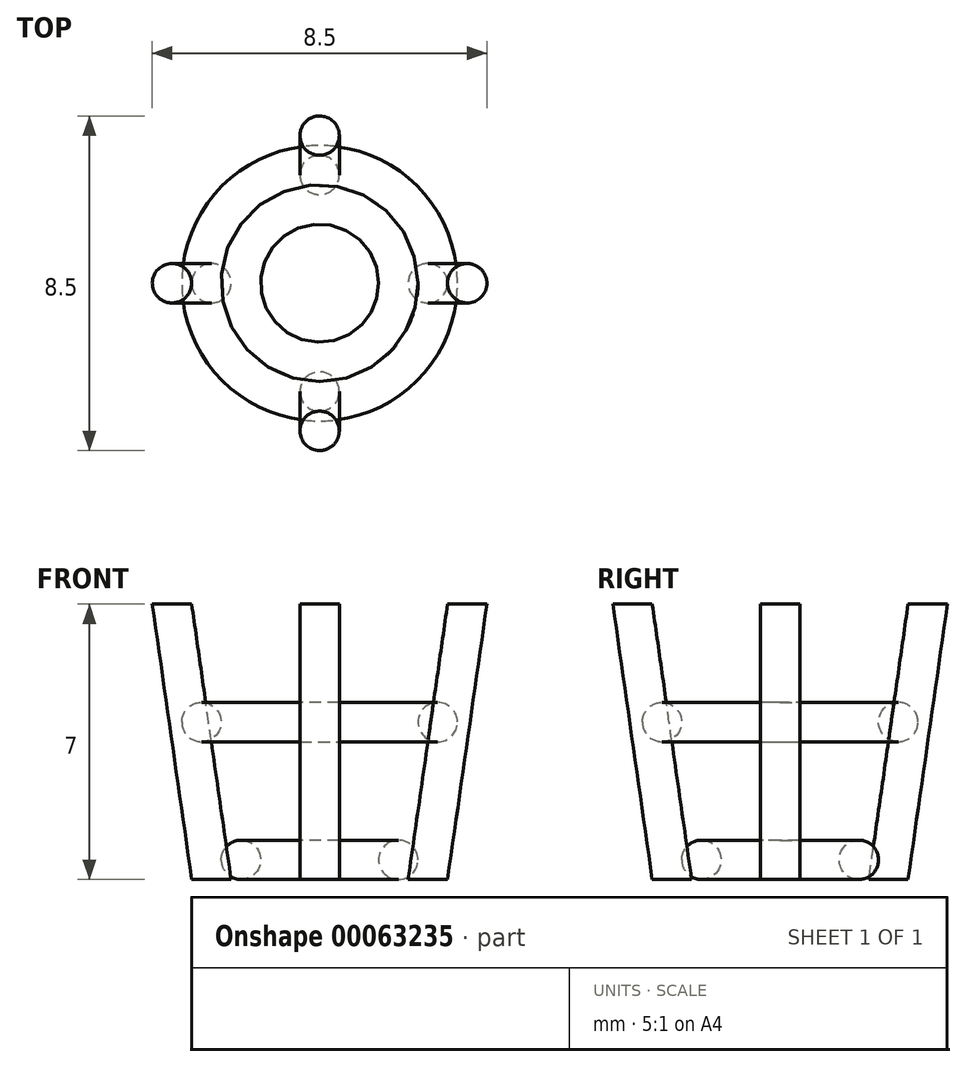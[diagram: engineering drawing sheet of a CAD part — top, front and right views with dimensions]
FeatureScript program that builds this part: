
annotation { "Feature Type Name" : "Feature", "Feature Type Description" : "" }
export const myFeature = defineFeature(function(context is Context, id is Id, definition is map)
    precondition{}
    {
        {
            var Q0;
            Q0=qCreatedBy(makeId("Front.planeOp"),FACE);
            var sketch = newSketch(context, id + "F0", { "sketchPlane" : qUnion([Q0])});
            skCircle(sketch, "E0", {"center": v(2, 0.5) * mm, "radius": 0.5 * mm});
            skCircle(sketch, "E1", {"center": v(3, 4) * mm, "radius": 0.5 * mm});
            skLineSegment(sketch, "E2", {"start": v(0, 7.83) * mm, "end": v(0, -6) * mm, "construction": true});
            skSolve(sketch);
        }
        {
            var Q0;
            Q0 = qSketchRegion(id + "F0", true);
            var Q1;
            Q1=sQuery(id+"F0.wireOp",EDGE,"E2");
            revolve(context, id + "F1", {"entities" : qUnion([Q0]), "axis" : qUnion([Q1]), "revolveType" : RevolveType.FULL});
        }
        {
            var Q0;
            Q0=qCreatedBy(makeId("Top.planeOp"),FACE);
            var sketch = newSketch(context, id + "F2", { "sketchPlane" : qUnion([Q0])});
            skCircle(sketch, "E3", {"center": v(2.75, 0) * mm, "radius": 0.5 * mm});
            skSolve(sketch);
        }
        {
            var Q0;
            Q0=qCreatedBy(makeId("Top.planeOp"),FACE);
            cPlane(context, id + "F3", {"entities" : qUnion([Q0]), "cplaneType" : CPlaneType.OFFSET, "offset" : 7 * mm, "width" : 150 * mm, "height" : 150 * mm});
        }
        {
            var Q0;
            Q0=qCreatedBy(id+"F3.planeOp",FACE);
            var sketch = newSketch(context, id + "F4", { "sketchPlane" : qUnion([Q0])});
            skCircle(sketch, "E4", {"center": v(3.75, 0) * mm, "radius": 0.5 * mm});
            skSolve(sketch);
        }
        {
            var Q0;
            Q0=makeQuery(id+"F4.imprint","IMPRINT",FACE,{"disambiguationData":[TD([[makeQuery(id+"F4.imprint","IMPRINT",EDGE,{"derivedFrom":sQuery(id+"F4.wireOp",EDGE,"E4")}),1.0]])]});
            var Q1;
            Q1=makeQuery(id+"F2.imprint","IMPRINT",FACE,{"disambiguationData":[TD([[makeQuery(id+"F2.imprint","IMPRINT",EDGE,{"derivedFrom":sQuery(id+"F2.wireOp",EDGE,"E3")}),1.0]])]});
            loft(context, id + "F5", {"sheetProfilesArray" : [{ "sheetProfileEntities" : qUnion([Q0]) }, { "sheetProfileEntities" : qUnion([Q1]) }]});
        }
        {
            var Q0;
            Q0=qCreatedBy(makeId("Front.planeOp"),FACE);
            var sketch = newSketch(context, id + "F6", { "sketchPlane" : qUnion([Q0])});
            skLineSegment(sketch, "E5", {"start": v(0, -1.44) * mm, "end": v(0, 8.4) * mm, "construction": true});
            skSolve(sketch);
        }
        {
            var Q0;
            Q0=makeQuery(id+"F5.opLoft","SWEPT_BODY",BODY,{"disambiguationData":[OSD([makeQuery(id+"F2.imprint","IMPRINT",FACE,{"disambiguationData":[TD([[makeQuery(id+"F2.imprint","IMPRINT",EDGE,{"derivedFrom":sQuery(id+"F2.wireOp",EDGE,"E3")}),1.0]])]}),makeQuery(id+"F4.imprint","IMPRINT",FACE,{"disambiguationData":[TD([[makeQuery(id+"F4.imprint","IMPRINT",EDGE,{"derivedFrom":sQuery(id+"F4.wireOp",EDGE,"E4")}),1.0]])]})])]});
            var Q1;
            Q1=sQuery(id+"F6.wireOp",EDGE,"E5");
            circularPattern(context, id + "F7", {"entities" : qUnion([Q0]), "axis" : qUnion([Q1]), "angle" : 360 * degree, "instanceCount" : 4, "equalSpace" : true});
        }
    });
